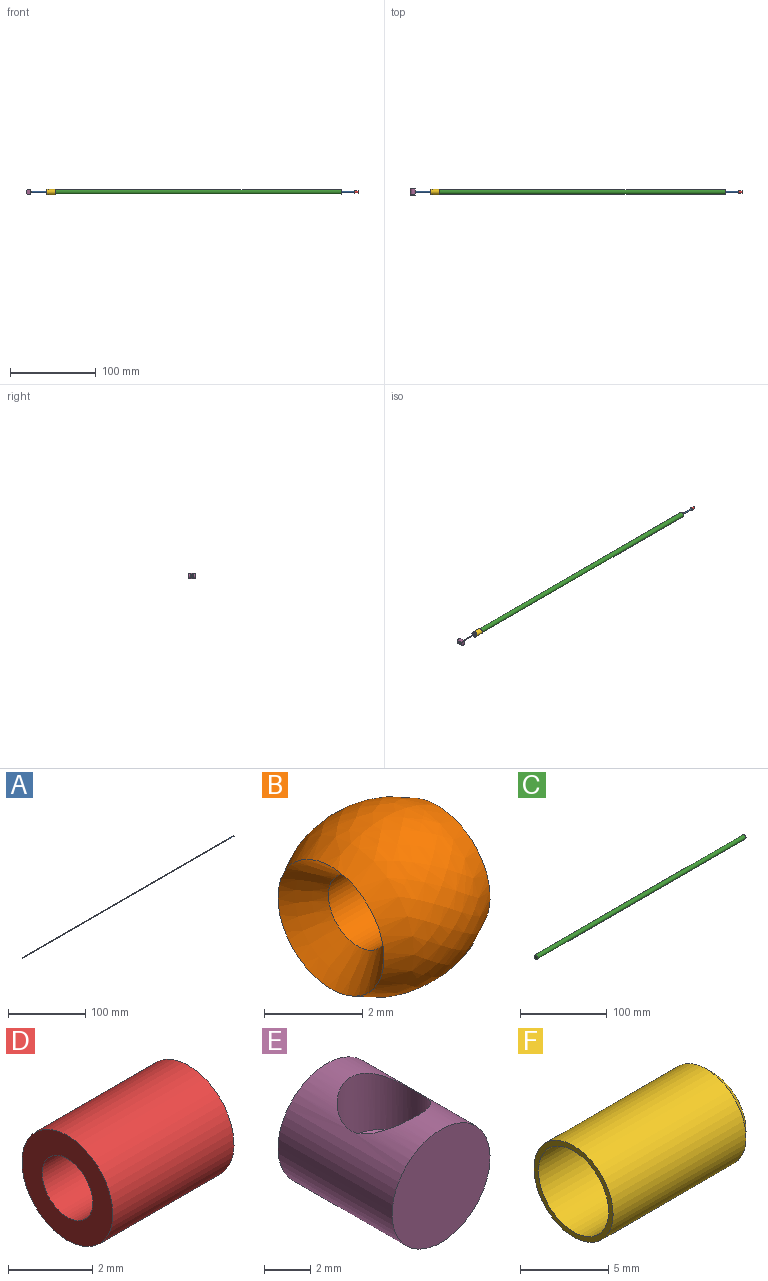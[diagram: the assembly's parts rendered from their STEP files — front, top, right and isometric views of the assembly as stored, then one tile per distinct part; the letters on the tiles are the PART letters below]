
ASSEMBLY  parts=6 mates=6
PART A: 3 faces, bbox 386x1.2x1.2 mm
  f0: plane 1.22x1.22mm, normal (-1,0,0), area 1.2mm2, adj f2
  f1: plane 1.22x1.22mm, normal (1,0,0), area 1.2mm2, adj f2
  f2: cylinder r=0.61mm len=386.03mm, axis (-1,0,0), area 1478.6mm2, adj f0,f1
PART B: 4 faces, bbox 3x4x4 mm
  f0: plane 3.05x3.05mm, normal (1,0,0), area 5mm2, adj f1,f2
  f1: revolved ~3.96x3.96mm, area 37.1mm2, adj f0,f3
  f2: cylinder r=0.85mm len=2.27mm, axis (-1,0,0), area 12.2mm2, adj f0,f3
  f3: cone r=0.85mm half-angle=41deg, axis (-1,0,0), area 7.7mm2, adj f1,f2
PART C: 3 faces, bbox 340.2x5.5x5.5 mm
  f0: plane 5.54x5.54mm, normal (-1,0,0), area 24.1mm2, adj f2
  f1: plane 5.54x5.54mm, normal (1,0,0), area 24.1mm2, adj f2
  f2: cylinder r=2.77mm len=340.23mm, axis (-1,0,0), area 5918.6mm2, adj f0,f1
PART D: 4 faces, bbox 4.1x3x3 mm
  f0: plane 3.05x3.05mm, normal (-1,0,0), area 5mm2, adj f2,f3
  f1: plane 3.05x3.05mm, normal (1,0,0), area 5mm2, adj f2,f3
  f2: cylinder r=1.52mm len=4.06mm, axis (-1,0,0), area 38.9mm2, adj f0,f1
  f3: cylinder r=0.85mm len=4.06mm, axis (-1,0,0), area 21.7mm2, adj f0,f1
PART E: 6 faces, bbox 6x7x6 mm
  f0: cone r=0mm half-angle=59deg, axis (0,0,1), area 11.8mm2, adj f3,f4
  f1: plane 5.99x5.99mm, normal (0,-1,0), area 28.2mm2, adj f5
  f2: plane 5.99x5.99mm, normal (0,1,0), area 28.2mm2, adj f5
  f3: cylinder r=2.03mm len=4.06mm, axis (0,0,1), area 35.7mm2, adj f0,f5
  f4: cylinder r=0.95mm len=2.17mm, axis (0,0,-1), area 12.5mm2, adj f0,f5
  f5: cylinder r=3mm len=6.99mm, axis (0,-1,0), area 114.8mm2, adj f1,f2,f3,f4
PART F: 7 faces, bbox 11.2x6.4x6.4 mm
  f0: cone r=0mm half-angle=59deg, axis (-1,0,0), area 24.3mm2, adj f4,f5
  f1: plane 6.35x6.35mm, normal (-1,0,0), area 6.7mm2, adj f3,f4
  f2: plane 5.33x5.33mm, normal (1,0,0), area 18.2mm2, adj f5,f6
  f3: cylinder r=3.17mm len=10.67mm, axis (-1,0,0), area 212.8mm2, adj f1,f6
  f4: cylinder r=2.82mm len=8.51mm, axis (-1,0,0), area 150.7mm2, adj f0,f1
  f5: cylinder r=1.14mm len=2.29mm, axis (1,0,0), area 11.9mm2, adj f0,f2
  f6: cone r=3.17mm half-angle=45deg, axis (-1,0,0), area 13.2mm2, adj f2,f3
PLACE A t=(-78.7,41.15,-32.16)mm
PLACE B t=(-78.7,41.15,-32.16)mm
PLACE C t=(-52.48,41.15,-32.16)mm
PLACE D t=(303.26,41.15,-32.16)mm
PLACE E rot(axis=(0.71,0,-0.71),180deg) t=(-72.84,37.66,-29.16)mm
PLACE F rot(axis=(0,1,0),180deg) t=(-43.97,41.15,-32.16)mm
MATE cylindrical F.f0 <-> C.f2  axis (1,0,0) through (-52.48,41.15,-32.16)mm
MATE cylindrical B.f2 <-> A.f2  axis (-1,0,0) through (-78.7,41.15,-32.16)mm
MATE cylindrical E.f0 <-> B.f2  axis (-1,0,0) through (-75.66,41.15,-32.16)mm
MATE cylindrical D.f2 <-> A.f2  axis (1,0,0) through (307.33,41.15,-32.16)mm
MATE cylindrical A.f2 <-> C.f2  axis (-1,0,0) through (-78.7,41.15,-32.16)mm
MATE cylindrical D.f2 <-> A.f2  axis (1,0,0) through (307.33,41.15,-32.16)mm
